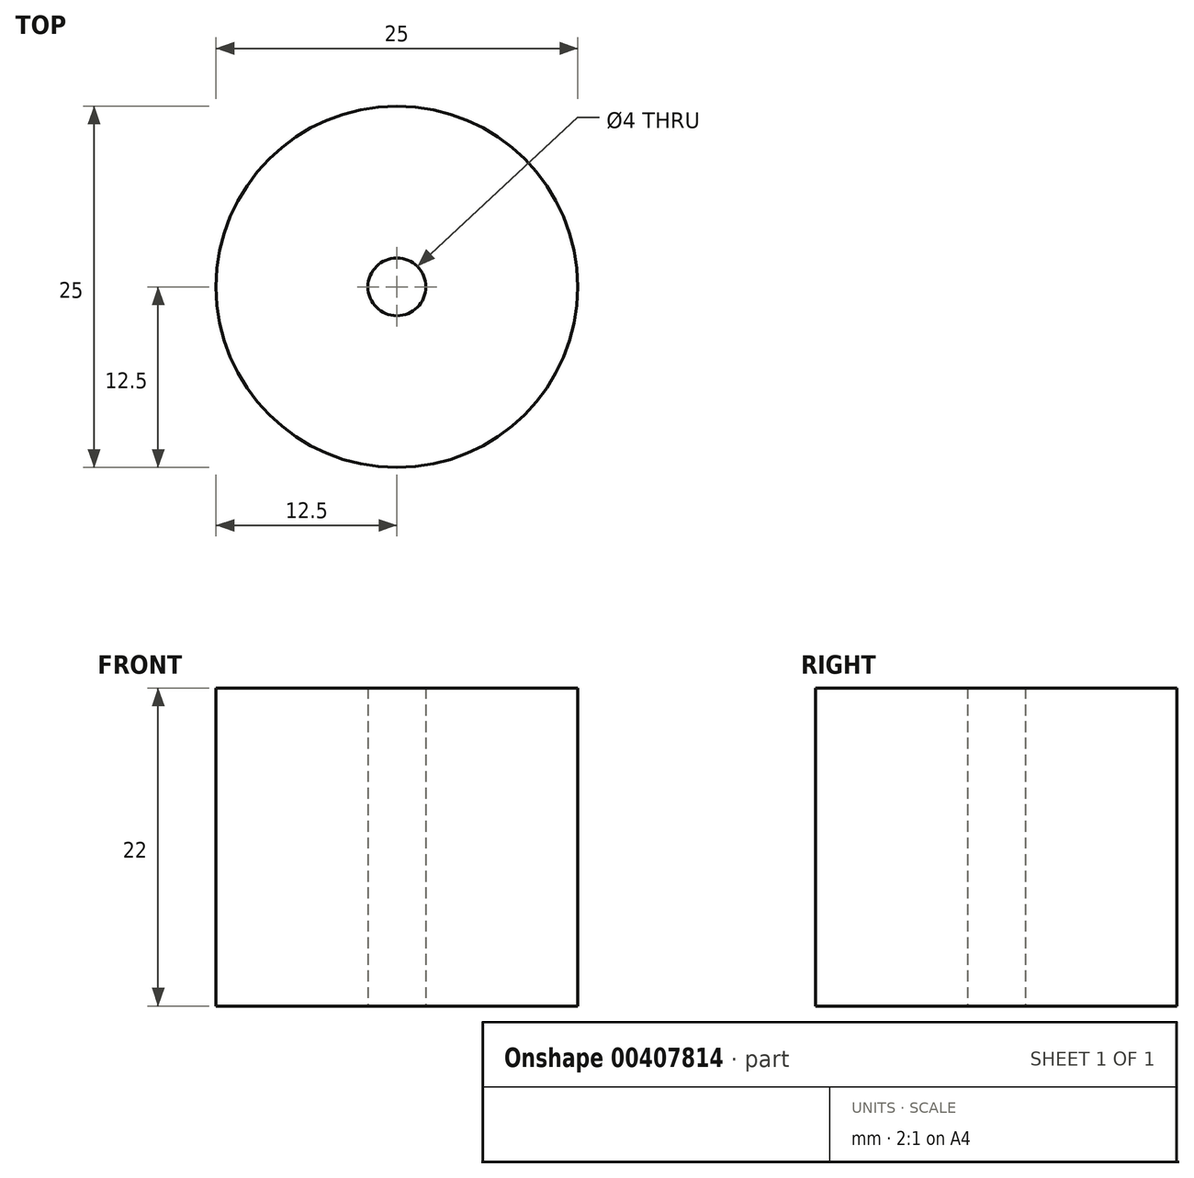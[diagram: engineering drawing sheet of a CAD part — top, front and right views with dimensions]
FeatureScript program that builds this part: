
annotation { "Feature Type Name" : "Feature", "Feature Type Description" : "" }
export const myFeature = defineFeature(function(context is Context, id is Id, definition is map)
    precondition{}
    {
        {
            var Q0;
            Q0=qCreatedBy(makeId("Top.planeOp"),FACE);
            var sketch = newSketch(context, id + "F0", { "sketchPlane" : qUnion([Q0])});
            skCircle(sketch, "E0", {"center": v(0, 0) * mm, "radius": 12.5 * mm});
            skCircle(sketch, "E1", {"center": v(0, 0) * mm, "radius": 2 * mm});
            skSolve(sketch);
        }
        {
            var Q0;
            Q0 = qSketchRegion(id + "F0", true);
            extrude(context, id + "F1", {"entities" : qUnion([Q0]), "depth" : 22 * mm});
        }
    });
